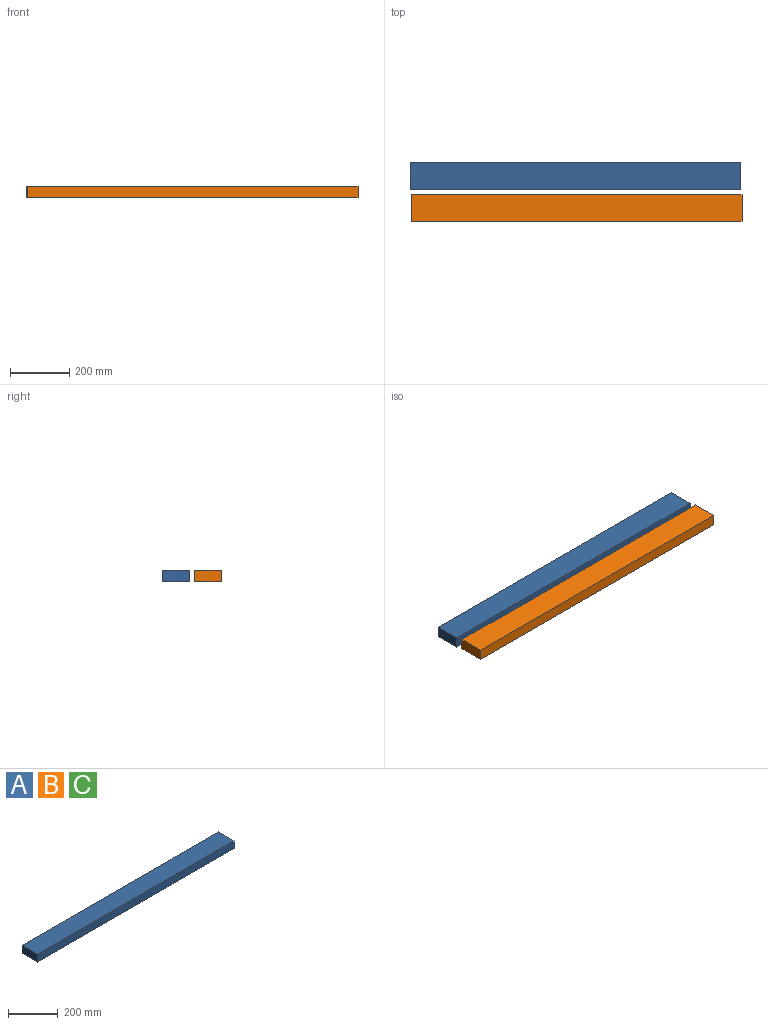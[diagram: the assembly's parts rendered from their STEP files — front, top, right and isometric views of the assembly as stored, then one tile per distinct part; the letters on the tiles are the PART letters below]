
ASSEMBLY  parts=3 mates=1
PART A: 6 faces, bbox 1117.6x88.9x38.1 mm
  f0: plane 1117.6x38.1mm, normal (0,1,0), area 42580.6mm2, adj f1,f3,f4,f5
  f1: plane 88.9x38.1mm, normal (-1,0,0), area 3387.1mm2, adj f0,f2,f4,f5
  f2: plane 1117.6x38.1mm, normal (0,-1,0), area 42580.6mm2, adj f1,f3,f4,f5
  f3: plane 88.9x38.1mm, normal (1,0,0), area 3387.1mm2, adj f0,f2,f4,f5
  f4: plane 1117.6x88.9mm, normal (0,0,1), area 99354.6mm2, adj f0,f1,f2,f3
  f5: plane 1117.6x88.9mm, normal (0,0,-1), area 99354.6mm2, adj f0,f1,f2,f3
PART B: same geometry as A
PART C: same geometry as A
PLACE A t=(-378.26,100.81,-19.08)mm
PLACE B t=(-371.84,-7.16,-19.62)mm
PLACE C t=(-378.26,100.81,-19.08)mm
MATE parallel A.f5 <-> C.f5  axis (0,0,-1) through (2.83,112.94,-19.08)mm
